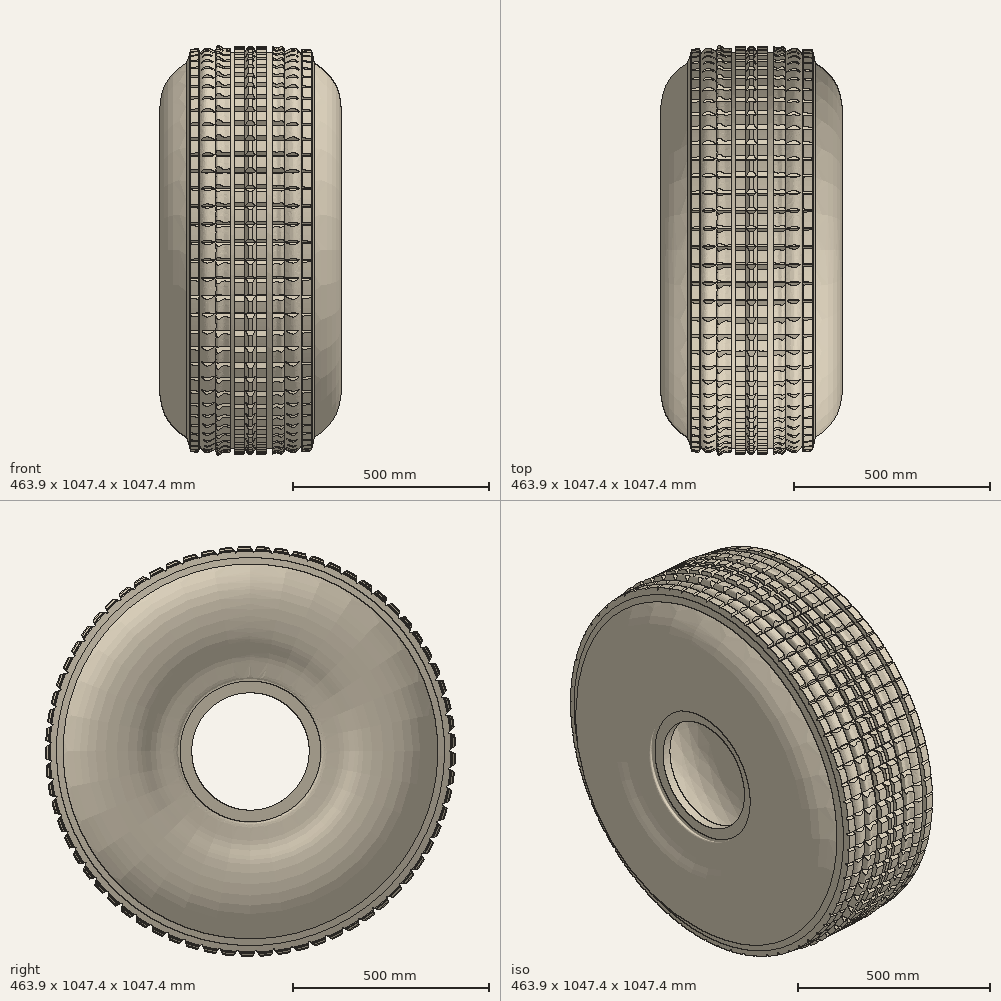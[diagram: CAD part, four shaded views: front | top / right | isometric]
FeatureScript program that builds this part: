
annotation { "Feature Type Name" : "Feature", "Feature Type Description" : "" }
export const myFeature = defineFeature(function(context is Context, id is Id, definition is map)
    precondition{}
    {
        {
            var Q0;
            Q0=qCreatedBy(makeId("Top.planeOp"),FACE);
            var sketch = newSketch(context, id + "F0", { "sketchPlane" : qUnion([Q0])});
            skPoint(sketch, "E0", {"position": v(-175, 150) * mm});
            skPoint(sketch, "E1", {"position": v(-150, 150) * mm});
            skLineSegment(sketch, "E2", {"start": v(-175, 150) * mm, "end": v(-150, 150) * mm});
            skPoint(sketch, "E3.MirrorP", {"position": v(150, 150) * mm});
            skPoint(sketch, "E4.MirrorP", {"position": v(175, 150) * mm});
            skLineSegment(sketch, "E5.MirrorCS", {"start": v(175, 150) * mm, "end": v(150, 150) * mm});
            skLineSegment(sketch, "E6", {"start": v(-175, 150) * mm, "end": v(-175, 180) * mm});
            skFitSpline(sketch, "E7", {"points": [v(-175, 180) * mm, v(-184.67, 184.02) * mm, v(-198.3, 234.45) * mm, v(-221.46, 282) * mm, v(-229.73, 382.86) * mm, v(-202.03, 445.7) * mm, v(-151.6, 486.2) * mm, v(0, 504.43) * mm], "startDerivative": vector(59.68, 901.94) * mm, "endDerivative": vector(1408.53, -72.4) * mm});
            skFitSpline(sketch, "E8", {"points": [v(0, 479.43) * mm, v(-134.36, 468.1) * mm, v(-182.95, 429.54) * mm, v(-201.89, 381.21) * mm, v(-198.6, 301.76) * mm, v(-176.16, 242.66) * mm, v(-163.87, 217.43) * mm, v(-150, 150) * mm], "startDerivative": vector(-727.82, -6.55) * mm, "endDerivative": vector(27.04, -741.2) * mm});
            skLineSegment(sketch, "E9.MirrorCS", {"start": v(175, 150) * mm, "end": v(175, 180) * mm});
            skFitSpline(sketch, "E10.MirrorCS", {"points": [v(175, 180) * mm, v(184.67, 184.02) * mm, v(198.3, 234.45) * mm, v(221.46, 282) * mm, v(229.73, 382.86) * mm, v(202.03, 445.7) * mm, v(151.6, 486.2) * mm, v(0, 504.43) * mm], "startDerivative": vector(-59.68, 901.94) * mm, "endDerivative": vector(-1408.53, -72.4) * mm});
            skFitSpline(sketch, "E11.MirrorCS", {"points": [v(0, 479.43) * mm, v(134.36, 468.1) * mm, v(182.95, 429.54) * mm, v(201.89, 381.21) * mm, v(198.6, 301.76) * mm, v(176.16, 242.66) * mm, v(163.87, 217.43) * mm, v(150, 150) * mm], "startDerivative": vector(727.82, -6.55) * mm, "endDerivative": vector(-27.04, -741.2) * mm});
            skLineSegment(sketch, "E12", {"start": v(-209.31, 0) * mm, "end": v(239.3, 0) * mm, "construction": true});
            skSolve(sketch);
        }
        {
            var Q0;
            Q0 = qSketchRegion(id + "F0", true);
            var Q1;
            Q1=sQuery(id+"F0.wireOp",EDGE,"E12");
            revolve(context, id + "F1", {"surfaceOperationType" : NewSurfaceOperationType.NEW, "entities" : qUnion([Q0]), "axis" : qUnion([Q1]), "revolveType" : RevolveType.FULL});
        }
        {
            var Q0;
            Q0=qCreatedBy(makeId("Top.planeOp"),FACE);
            var sketch = newSketch(context, id + "F2", { "sketchPlane" : qUnion([Q0])});
            skLineSegment(sketch, "E13.bottom", {"start": v(-130, 496.95) * mm, "end": v(-130, 496.95) * mm});
            skFitSpline(sketch, "E14", {"points": [v(-117.15, 514.71) * mm, v(-130, 496.95) * mm, v(-119.3, 500.26) * mm, v(-92.18, 504.71) * mm, v(-90.25, 504.85) * mm, v(-85.06, 505) * mm, v(-88.83, 507.25) * mm, v(-98.38, 513.06) * mm, v(-117.15, 514.71) * mm]});
            skLineSegment(sketch, "E15.MirrorCS", {"start": v(-40.33, 499.33) * mm, "end": v(-40.38, 521.13) * mm});
            skLineSegment(sketch, "E16.MirrorCS", {"start": v(-15, 499.38) * mm, "end": v(-14.97, 521.11) * mm});
            skLineSegment(sketch, "E17.MirrorCS", {"start": v(-40.33, 499.33) * mm, "end": v(-15, 499.38) * mm});
            skFitSpline(sketch, "E18.MirrorC", {"points": [v(-52.4, 516.54) * mm, v(-51.02, 508.2) * mm, v(-49.36, 501.85) * mm, v(-40.33, 499.33) * mm, v(-85.06, 505) * mm, v(-82.79, 523.58) * mm, v(-68.13, 515.76) * mm, v(-52.4, 516.54) * mm]});
            skLineSegment(sketch, "E19.MirrorCS", {"start": v(-40.38, 521.13) * mm, "end": v(-14.97, 521.11) * mm});
            skFitSpline(sketch, "E20.MirrorC", {"points": [v(55.63, 520.93) * mm, v(55.22, 506.03) * mm, v(40.33, 499.33) * mm, v(44.42, 498.82) * mm, v(85.82, 502.74) * mm, v(81.28, 520.6) * mm, v(67.8, 517.23) * mm, v(55.63, 520.93) * mm]});
            skPoint(sketch, "E21", {"position": v(130, 496.95) * mm});
            skLineSegment(sketch, "E22", {"start": v(-163.32, 478.74) * mm, "end": v(-156.87, 496.6) * mm});
            skLineSegment(sketch, "E23", {"start": v(-156.87, 496.6) * mm, "end": v(-152.6, 513.75) * mm});
            skLineSegment(sketch, "E24", {"start": v(-130, 496.95) * mm, "end": v(-163.32, 478.74) * mm});
            skLineSegment(sketch, "E25.MirrorCS", {"start": v(159.55, 495.78) * mm, "end": v(155.7, 512.1) * mm});
            skLineSegment(sketch, "E26.MirrorCS", {"start": v(163.38, 478.68) * mm, "end": v(159.55, 495.78) * mm});
            skLineSegment(sketch, "E27.MirrorCS", {"start": v(130, 496.95) * mm, "end": v(131.74, 514.48) * mm});
            skLineSegment(sketch, "E28.MirrorCS", {"start": v(130, 496.95) * mm, "end": v(163.38, 478.68) * mm});
            skFitSpline(sketch, "E29.MirrorC", {"points": [v(117.3, 514.36) * mm, v(130, 496.95) * mm, v(119.31, 500.29) * mm, v(107.79, 499.28) * mm, v(91.02, 502) * mm, v(87.1, 505.2) * mm, v(98.36, 513.14) * mm, v(117.3, 514.36) * mm]});
            skLineSegment(sketch, "E30", {"start": v(-15, 505.05) * mm, "end": v(-15, 499.38) * mm});
            skLineSegment(sketch, "E31", {"start": v(-15, 505.05) * mm, "end": v(-5.43, 520.92) * mm});
            skLineSegment(sketch, "E32", {"start": v(-5.43, 520.92) * mm, "end": v(5.22, 520.9) * mm});
            skLineSegment(sketch, "E33", {"start": v(5.22, 520.9) * mm, "end": v(15, 504.77) * mm});
            skLineSegment(sketch, "E34", {"start": v(15, 504.77) * mm, "end": v(0, 500.87) * mm});
            skLineSegment(sketch, "E35", {"start": v(0, 500.87) * mm, "end": v(-15, 505.05) * mm});
            skLineSegment(sketch, "E36.MirrorCS", {"start": v(15, 505.05) * mm, "end": v(15, 499.38) * mm});
            skLineSegment(sketch, "E37.MirrorCS", {"start": v(40.38, 521.13) * mm, "end": v(14.97, 521.11) * mm});
            skLineSegment(sketch, "E38.MirrorCS", {"start": v(40.33, 499.33) * mm, "end": v(15, 499.38) * mm});
            skLineSegment(sketch, "E39.MirrorCS", {"start": v(40.33, 499.33) * mm, "end": v(40.38, 521.13) * mm});
            skLineSegment(sketch, "E40.MirrorCS", {"start": v(15, 499.38) * mm, "end": v(14.97, 521.11) * mm});
            skLineSegment(sketch, "E41", {"start": v(-152.6, 513.75) * mm, "end": v(-132.3, 516.19) * mm});
            skLineSegment(sketch, "E42", {"start": v(-132.3, 516.19) * mm, "end": v(-130, 496.95) * mm});
            skLineSegment(sketch, "E43", {"start": v(131.74, 514.48) * mm, "end": v(155.7, 512.1) * mm});
            skSolve(sketch);
        }
        {
            var Q0;
            Q0 = qSketchRegion(id + "F2", true);
            var Q1;
            Q1=sQuery(id+"F0.wireOp",EDGE,"E12");
            revolve(context, id + "F3", {"operationType" : NewBodyOperationType.ADD, "surfaceOperationType" : NewSurfaceOperationType.NEW, "entities" : qUnion([Q0]), "axis" : qUnion([Q1]), "revolveType" : RevolveType.FULL});
        }
        {
            var Q0;
            Q0=qCreatedBy(makeId("Right.planeOp"),FACE);
            var sketch = newSketch(context, id + "F4", { "sketchPlane" : qUnion([Q0])});
            skLineSegment(sketch, "E44", {"start": v(532.3, 38.8) * mm, "end": v(504.85, 47.75) * mm});
            skLineSegment(sketch, "E45", {"start": v(504.85, 47.75) * mm, "end": v(526.33, 67.04) * mm});
            skLineSegment(sketch, "E46", {"start": v(526.33, 67.04) * mm, "end": v(532.3, 38.8) * mm});
            skPoint(sketch, "E47", {"position": v(504.85, 47.75) * mm});
            skLineSegment(sketch, "E48.1.0", {"start": v(526.56, 87.04) * mm, "end": v(498.42, 93.46) * mm});
            skLineSegment(sketch, "E48.1.1", {"start": v(498.42, 93.46) * mm, "end": v(518.05, 114.62) * mm});
            skLineSegment(sketch, "E48.1.2", {"start": v(518.05, 114.62) * mm, "end": v(526.56, 87.04) * mm});
            skLineSegment(sketch, "E48.2.0", {"start": v(516.47, 134.56) * mm, "end": v(487.86, 138.4) * mm});
            skLineSegment(sketch, "E48.2.1", {"start": v(487.86, 138.4) * mm, "end": v(505.48, 161.26) * mm});
            skLineSegment(sketch, "E48.2.2", {"start": v(505.48, 161.26) * mm, "end": v(516.47, 134.56) * mm});
            skLineSegment(sketch, "E48.3.0", {"start": v(502.1, 180.97) * mm, "end": v(473.25, 182.18) * mm});
            skLineSegment(sketch, "E48.3.1", {"start": v(473.25, 182.18) * mm, "end": v(488.72, 206.55) * mm});
            skLineSegment(sketch, "E48.3.2", {"start": v(488.72, 206.55) * mm, "end": v(502.1, 180.97) * mm});
            skLineSegment(sketch, "E48.4.0", {"start": v(483.56, 225.88) * mm, "end": v(454.72, 224.46) * mm});
            skLineSegment(sketch, "E48.4.1", {"start": v(454.72, 224.46) * mm, "end": v(467.92, 250.14) * mm});
            skLineSegment(sketch, "E48.4.2", {"start": v(467.92, 250.14) * mm, "end": v(483.56, 225.88) * mm});
            skLineSegment(sketch, "E48.5.0", {"start": v(461.01, 268.91) * mm, "end": v(432.43, 264.88) * mm});
            skLineSegment(sketch, "E48.5.1", {"start": v(432.43, 264.88) * mm, "end": v(443.23, 291.65) * mm});
            skLineSegment(sketch, "E48.5.2", {"start": v(443.23, 291.65) * mm, "end": v(461.01, 268.91) * mm});
            skLineSegment(sketch, "E48.6.0", {"start": v(434.65, 309.72) * mm, "end": v(406.55, 303.11) * mm});
            skLineSegment(sketch, "E48.6.1", {"start": v(406.55, 303.11) * mm, "end": v(414.87, 330.75) * mm});
            skLineSegment(sketch, "E48.6.2", {"start": v(414.87, 330.75) * mm, "end": v(434.65, 309.72) * mm});
            skLineSegment(sketch, "E48.7.0", {"start": v(404.68, 347.96) * mm, "end": v(377.3, 338.82) * mm});
            skLineSegment(sketch, "E48.7.1", {"start": v(377.3, 338.82) * mm, "end": v(383.08, 367.1) * mm});
            skLineSegment(sketch, "E48.7.2", {"start": v(383.08, 367.1) * mm, "end": v(404.68, 347.96) * mm});
            skLineSegment(sketch, "E48.8.0", {"start": v(371.36, 383.32) * mm, "end": v(344.93, 371.73) * mm});
            skLineSegment(sketch, "E48.8.1", {"start": v(344.93, 371.73) * mm, "end": v(348.1, 400.42) * mm});
            skLineSegment(sketch, "E48.8.2", {"start": v(348.1, 400.42) * mm, "end": v(371.36, 383.32) * mm});
            skLineSegment(sketch, "E48.9.0", {"start": v(334.97, 415.5) * mm, "end": v(309.7, 401.56) * mm});
            skLineSegment(sketch, "E48.9.1", {"start": v(309.7, 401.56) * mm, "end": v(310.25, 430.42) * mm});
            skLineSegment(sketch, "E48.9.2", {"start": v(310.25, 430.42) * mm, "end": v(334.97, 415.5) * mm});
            skLineSegment(sketch, "E48.10.0", {"start": v(295.8, 444.24) * mm, "end": v(271.9, 428.05) * mm});
            skLineSegment(sketch, "E48.10.1", {"start": v(271.9, 428.05) * mm, "end": v(269.83, 456.85) * mm});
            skLineSegment(sketch, "E48.10.2", {"start": v(269.83, 456.85) * mm, "end": v(295.8, 444.24) * mm});
            skLineSegment(sketch, "E48.11.0", {"start": v(254.18, 469.3) * mm, "end": v(231.84, 451) * mm});
            skLineSegment(sketch, "E48.11.1", {"start": v(231.84, 451) * mm, "end": v(227.17, 479.5) * mm});
            skLineSegment(sketch, "E48.11.2", {"start": v(227.17, 479.5) * mm, "end": v(254.18, 469.3) * mm});
            skLineSegment(sketch, "E48.12.0", {"start": v(210.45, 490.47) * mm, "end": v(189.87, 470.22) * mm});
            skLineSegment(sketch, "E48.12.1", {"start": v(189.87, 470.22) * mm, "end": v(182.62, 498.16) * mm});
            skLineSegment(sketch, "E48.12.2", {"start": v(182.62, 498.16) * mm, "end": v(210.45, 490.47) * mm});
            skLineSegment(sketch, "E48.13.0", {"start": v(164.97, 507.57) * mm, "end": v(146.33, 485.54) * mm});
            skLineSegment(sketch, "E48.13.1", {"start": v(146.33, 485.54) * mm, "end": v(136.57, 512.7) * mm});
            skLineSegment(sketch, "E48.13.2", {"start": v(136.57, 512.7) * mm, "end": v(164.97, 507.57) * mm});
            skLineSegment(sketch, "E48.14.0", {"start": v(118.13, 520.47) * mm, "end": v(101.57, 496.83) * mm});
            skLineSegment(sketch, "E48.14.1", {"start": v(101.57, 496.83) * mm, "end": v(89.38, 523) * mm});
            skLineSegment(sketch, "E48.14.2", {"start": v(89.38, 523) * mm, "end": v(118.13, 520.47) * mm});
            skLineSegment(sketch, "E48.15.0", {"start": v(70.32, 529.06) * mm, "end": v(55.97, 504) * mm});
            skLineSegment(sketch, "E48.15.1", {"start": v(55.97, 504) * mm, "end": v(41.45, 528.96) * mm});
            skLineSegment(sketch, "E48.15.2", {"start": v(41.45, 528.96) * mm, "end": v(70.32, 529.06) * mm});
            skLineSegment(sketch, "E48.16.0", {"start": v(21.91, 533.26) * mm, "end": v(9.9, 507) * mm});
            skLineSegment(sketch, "E48.16.1", {"start": v(9.9, 507) * mm, "end": v(-6.82, 530.54) * mm});
            skLineSegment(sketch, "E48.16.2", {"start": v(-6.82, 530.54) * mm, "end": v(21.91, 533.26) * mm});
            skLineSegment(sketch, "E48.17.0", {"start": v(-26.67, 533.04) * mm, "end": v(-36.24, 505.8) * mm});
            skLineSegment(sketch, "E48.17.1", {"start": v(-36.24, 505.8) * mm, "end": v(-55.04, 527.72) * mm});
            skLineSegment(sketch, "E48.17.2", {"start": v(-55.04, 527.72) * mm, "end": v(-26.67, 533.04) * mm});
            skLineSegment(sketch, "E48.18.0", {"start": v(-75.03, 528.4) * mm, "end": v(-82.09, 500.42) * mm});
            skLineSegment(sketch, "E48.18.1", {"start": v(-82.09, 500.42) * mm, "end": v(-102.8, 520.53) * mm});
            skLineSegment(sketch, "E48.18.2", {"start": v(-102.8, 520.53) * mm, "end": v(-75.03, 528.4) * mm});
            skLineSegment(sketch, "E48.19.0", {"start": v(-122.77, 519.4) * mm, "end": v(-127.25, 490.88) * mm});
            skLineSegment(sketch, "E48.19.1", {"start": v(-127.25, 490.88) * mm, "end": v(-149.7, 509.02) * mm});
            skLineSegment(sketch, "E48.19.2", {"start": v(-149.7, 509.02) * mm, "end": v(-122.77, 519.4) * mm});
            skLineSegment(sketch, "E48.20.0", {"start": v(-169.5, 506.08) * mm, "end": v(-171.36, 477.27) * mm});
            skLineSegment(sketch, "E48.20.1", {"start": v(-171.36, 477.27) * mm, "end": v(-195.38, 493.3) * mm});
            skLineSegment(sketch, "E48.20.2", {"start": v(-195.38, 493.3) * mm, "end": v(-169.5, 506.08) * mm});
            skLineSegment(sketch, "E48.21.0", {"start": v(-214.81, 488.57) * mm, "end": v(-214.06, 459.71) * mm});
            skLineSegment(sketch, "E48.21.1", {"start": v(-214.06, 459.71) * mm, "end": v(-239.42, 473.49) * mm});
            skLineSegment(sketch, "E48.21.2", {"start": v(-239.42, 473.49) * mm, "end": v(-214.81, 488.57) * mm});
            skLineSegment(sketch, "E48.22.0", {"start": v(-258.35, 467.01) * mm, "end": v(-254.97, 438.34) * mm});
            skLineSegment(sketch, "E48.22.1", {"start": v(-254.97, 438.34) * mm, "end": v(-281.49, 449.76) * mm});
            skLineSegment(sketch, "E48.22.2", {"start": v(-281.49, 449.76) * mm, "end": v(-258.35, 467.01) * mm});
            skLineSegment(sketch, "E48.23.0", {"start": v(-299.75, 441.59) * mm, "end": v(-293.78, 413.34) * mm});
            skLineSegment(sketch, "E48.23.1", {"start": v(-293.78, 413.34) * mm, "end": v(-321.22, 422.3) * mm});
            skLineSegment(sketch, "E48.23.2", {"start": v(-321.22, 422.3) * mm, "end": v(-299.75, 441.59) * mm});
            skLineSegment(sketch, "E48.24.0", {"start": v(-338.66, 412.5) * mm, "end": v(-330.15, 384.92) * mm});
            skLineSegment(sketch, "E48.24.1", {"start": v(-330.15, 384.92) * mm, "end": v(-358.3, 391.34) * mm});
            skLineSegment(sketch, "E48.24.2", {"start": v(-358.3, 391.34) * mm, "end": v(-338.66, 412.5) * mm});
            skLineSegment(sketch, "E48.25.0", {"start": v(-374.77, 380) * mm, "end": v(-363.78, 353.3) * mm});
            skLineSegment(sketch, "E48.25.1", {"start": v(-363.78, 353.3) * mm, "end": v(-392.4, 357.13) * mm});
            skLineSegment(sketch, "E48.25.2", {"start": v(-392.4, 357.13) * mm, "end": v(-374.77, 380) * mm});
            skLineSegment(sketch, "E48.26.0", {"start": v(-407.77, 344.34) * mm, "end": v(-394.4, 318.75) * mm});
            skLineSegment(sketch, "E48.26.1", {"start": v(-394.4, 318.75) * mm, "end": v(-423.24, 319.97) * mm});
            skLineSegment(sketch, "E48.26.2", {"start": v(-423.24, 319.97) * mm, "end": v(-407.77, 344.34) * mm});
            skLineSegment(sketch, "E48.27.0", {"start": v(-437.4, 305.83) * mm, "end": v(-421.75, 281.57) * mm});
            skLineSegment(sketch, "E48.27.1", {"start": v(-421.75, 281.57) * mm, "end": v(-450.59, 280.16) * mm});
            skLineSegment(sketch, "E48.27.2", {"start": v(-450.59, 280.16) * mm, "end": v(-437.4, 305.83) * mm});
            skLineSegment(sketch, "E48.28.0", {"start": v(-463.4, 264.8) * mm, "end": v(-445.61, 242.05) * mm});
            skLineSegment(sketch, "E48.28.1", {"start": v(-445.61, 242.05) * mm, "end": v(-474.2, 238.02) * mm});
            skLineSegment(sketch, "E48.28.2", {"start": v(-474.2, 238.02) * mm, "end": v(-463.4, 264.8) * mm});
            skLineSegment(sketch, "E48.29.0", {"start": v(-485.55, 221.56) * mm, "end": v(-465.78, 200.53) * mm});
            skLineSegment(sketch, "E48.29.1", {"start": v(-465.78, 200.53) * mm, "end": v(-493.88, 193.92) * mm});
            skLineSegment(sketch, "E48.29.2", {"start": v(-493.88, 193.92) * mm, "end": v(-485.55, 221.56) * mm});
            skLineSegment(sketch, "E48.30.0", {"start": v(-503.69, 176.49) * mm, "end": v(-482.08, 157.34) * mm});
            skLineSegment(sketch, "E48.30.1", {"start": v(-482.08, 157.34) * mm, "end": v(-509.46, 148.2) * mm});
            skLineSegment(sketch, "E48.30.2", {"start": v(-509.46, 148.2) * mm, "end": v(-503.69, 176.49) * mm});
            skLineSegment(sketch, "E48.31.0", {"start": v(-517.65, 129.95) * mm, "end": v(-494.4, 112.85) * mm});
            skLineSegment(sketch, "E48.31.1", {"start": v(-494.4, 112.85) * mm, "end": v(-520.83, 101.26) * mm});
            skLineSegment(sketch, "E48.31.2", {"start": v(-520.83, 101.26) * mm, "end": v(-517.65, 129.95) * mm});
            skLineSegment(sketch, "E48.32.0", {"start": v(-527.32, 82.34) * mm, "end": v(-502.6, 67.43) * mm});
            skLineSegment(sketch, "E48.32.1", {"start": v(-502.6, 67.43) * mm, "end": v(-527.88, 53.48) * mm});
            skLineSegment(sketch, "E48.32.2", {"start": v(-527.88, 53.48) * mm, "end": v(-527.32, 82.34) * mm});
            skLineSegment(sketch, "E48.33.0", {"start": v(-532.62, 34.05) * mm, "end": v(-506.65, 21.44) * mm});
            skLineSegment(sketch, "E48.33.1", {"start": v(-506.65, 21.44) * mm, "end": v(-530.56, 5.25) * mm});
            skLineSegment(sketch, "E48.33.2", {"start": v(-530.56, 5.25) * mm, "end": v(-532.62, 34.05) * mm});
            skLineSegment(sketch, "E48.34.0", {"start": v(-533.51, -14.53) * mm, "end": v(-506.5, -24.72) * mm});
            skLineSegment(sketch, "E48.34.1", {"start": v(-506.5, -24.72) * mm, "end": v(-528.83, -43.01) * mm});
            skLineSegment(sketch, "E48.34.2", {"start": v(-528.83, -43.01) * mm, "end": v(-533.51, -14.53) * mm});
            skLineSegment(sketch, "E48.35.0", {"start": v(-529.98, -62.98) * mm, "end": v(-502.16, -70.68) * mm});
            skLineSegment(sketch, "E48.35.1", {"start": v(-502.16, -70.68) * mm, "end": v(-522.73, -90.92) * mm});
            skLineSegment(sketch, "E48.35.2", {"start": v(-522.73, -90.92) * mm, "end": v(-529.98, -62.98) * mm});
            skLineSegment(sketch, "E48.36.0", {"start": v(-522.06, -110.91) * mm, "end": v(-493.65, -116.05) * mm});
            skLineSegment(sketch, "E48.36.1", {"start": v(-493.65, -116.05) * mm, "end": v(-512.3, -138.08) * mm});
            skLineSegment(sketch, "E48.36.2", {"start": v(-512.3, -138.08) * mm, "end": v(-522.06, -110.91) * mm});
            skLineSegment(sketch, "E48.37.0", {"start": v(-509.8, -157.93) * mm, "end": v(-481.05, -160.46) * mm});
            skLineSegment(sketch, "E48.37.1", {"start": v(-481.05, -160.46) * mm, "end": v(-497.62, -184.1) * mm});
            skLineSegment(sketch, "E48.37.2", {"start": v(-497.62, -184.1) * mm, "end": v(-509.8, -157.93) * mm});
            skLineSegment(sketch, "E48.38.0", {"start": v(-493.34, -203.63) * mm, "end": v(-464.47, -203.54) * mm});
            skLineSegment(sketch, "E48.38.1", {"start": v(-464.47, -203.54) * mm, "end": v(-478.82, -228.58) * mm});
            skLineSegment(sketch, "E48.38.2", {"start": v(-478.82, -228.58) * mm, "end": v(-493.34, -203.63) * mm});
            skLineSegment(sketch, "E48.39.0", {"start": v(-472.77, -247.65) * mm, "end": v(-444.03, -244.93) * mm});
            skLineSegment(sketch, "E48.39.1", {"start": v(-444.03, -244.93) * mm, "end": v(-456.05, -271.18) * mm});
            skLineSegment(sketch, "E48.39.2", {"start": v(-456.05, -271.18) * mm, "end": v(-472.77, -247.65) * mm});
            skLineSegment(sketch, "E48.40.0", {"start": v(-448.3, -289.62) * mm, "end": v(-419.92, -284.3) * mm});
            skLineSegment(sketch, "E48.40.1", {"start": v(-419.92, -284.3) * mm, "end": v(-429.5, -311.53) * mm});
            skLineSegment(sketch, "E48.40.2", {"start": v(-429.5, -311.53) * mm, "end": v(-448.3, -289.62) * mm});
            skLineSegment(sketch, "E48.41.0", {"start": v(-420.1, -329.18) * mm, "end": v(-392.33, -321.3) * mm});
            skLineSegment(sketch, "E48.41.1", {"start": v(-392.33, -321.3) * mm, "end": v(-399.39, -349.3) * mm});
            skLineSegment(sketch, "E48.41.2", {"start": v(-399.39, -349.3) * mm, "end": v(-420.1, -329.18) * mm});
            skLineSegment(sketch, "E48.42.0", {"start": v(-388.43, -366.02) * mm, "end": v(-361.49, -355.65) * mm});
            skLineSegment(sketch, "E48.42.1", {"start": v(-361.49, -355.65) * mm, "end": v(-365.97, -384.16) * mm});
            skLineSegment(sketch, "E48.42.2", {"start": v(-365.97, -384.16) * mm, "end": v(-388.43, -366.02) * mm});
            skLineSegment(sketch, "E48.43.0", {"start": v(-353.53, -399.83) * mm, "end": v(-327.65, -387.04) * mm});
            skLineSegment(sketch, "E48.43.1", {"start": v(-327.65, -387.04) * mm, "end": v(-329.52, -415.85) * mm});
            skLineSegment(sketch, "E48.43.2", {"start": v(-329.52, -415.85) * mm, "end": v(-353.53, -399.83) * mm});
            skLineSegment(sketch, "E48.44.0", {"start": v(-315.71, -430.32) * mm, "end": v(-291.1, -415.23) * mm});
            skLineSegment(sketch, "E48.44.1", {"start": v(-291.1, -415.23) * mm, "end": v(-290.34, -444.1) * mm});
            skLineSegment(sketch, "E48.44.2", {"start": v(-290.34, -444.1) * mm, "end": v(-315.71, -430.32) * mm});
            skLineSegment(sketch, "E48.45.0", {"start": v(-275.27, -457.24) * mm, "end": v(-252.13, -439.99) * mm});
            skLineSegment(sketch, "E48.45.1", {"start": v(-252.13, -439.99) * mm, "end": v(-248.76, -468.65) * mm});
            skLineSegment(sketch, "E48.45.2", {"start": v(-248.76, -468.65) * mm, "end": v(-275.27, -457.24) * mm});
            skLineSegment(sketch, "E48.46.0", {"start": v(-232.55, -480.38) * mm, "end": v(-211.08, -461.09) * mm});
            skLineSegment(sketch, "E48.46.1", {"start": v(-211.08, -461.09) * mm, "end": v(-205.1, -489.33) * mm});
            skLineSegment(sketch, "E48.46.2", {"start": v(-205.1, -489.33) * mm, "end": v(-232.55, -480.38) * mm});
            skLineSegment(sketch, "E48.47.0", {"start": v(-187.9, -499.54) * mm, "end": v(-168.27, -478.37) * mm});
            skLineSegment(sketch, "E48.47.1", {"start": v(-168.27, -478.37) * mm, "end": v(-159.76, -505.96) * mm});
            skLineSegment(sketch, "E48.47.2", {"start": v(-159.76, -505.96) * mm, "end": v(-187.9, -499.54) * mm});
            skLineSegment(sketch, "E48.48.0", {"start": v(-141.7, -514.55) * mm, "end": v(-124.07, -491.7) * mm});
            skLineSegment(sketch, "E48.48.1", {"start": v(-124.07, -491.7) * mm, "end": v(-113.09, -518.39) * mm});
            skLineSegment(sketch, "E48.48.2", {"start": v(-113.09, -518.39) * mm, "end": v(-141.7, -514.55) * mm});
            skLineSegment(sketch, "E48.49.0", {"start": v(-94.32, -525.3) * mm, "end": v(-78.85, -500.94) * mm});
            skLineSegment(sketch, "E48.49.1", {"start": v(-78.85, -500.94) * mm, "end": v(-65.48, -526.52) * mm});
            skLineSegment(sketch, "E48.49.2", {"start": v(-65.48, -526.52) * mm, "end": v(-94.32, -525.3) * mm});
            skLineSegment(sketch, "E48.50.0", {"start": v(-46.16, -531.7) * mm, "end": v(-32.97, -506.03) * mm});
            skLineSegment(sketch, "E48.50.1", {"start": v(-32.97, -506.03) * mm, "end": v(-17.33, -530.3) * mm});
            skLineSegment(sketch, "E48.50.2", {"start": v(-17.33, -530.3) * mm, "end": v(-46.16, -531.7) * mm});
            skLineSegment(sketch, "E48.51.0", {"start": v(2.38, -533.7) * mm, "end": v(13.18, -506.94) * mm});
            skLineSegment(sketch, "E48.51.1", {"start": v(13.18, -506.94) * mm, "end": v(30.96, -529.68) * mm});
            skLineSegment(sketch, "E48.51.2", {"start": v(30.96, -529.68) * mm, "end": v(2.38, -533.7) * mm});
            skLineSegment(sketch, "E48.52.0", {"start": v(50.9, -531.28) * mm, "end": v(59.23, -503.64) * mm});
            skLineSegment(sketch, "E48.52.1", {"start": v(59.23, -503.64) * mm, "end": v(79, -524.67) * mm});
            skLineSegment(sketch, "E48.52.2", {"start": v(79, -524.67) * mm, "end": v(50.9, -531.28) * mm});
            skLineSegment(sketch, "E48.53.0", {"start": v(99, -524.45) * mm, "end": v(104.78, -496.16) * mm});
            skLineSegment(sketch, "E48.53.1", {"start": v(104.78, -496.16) * mm, "end": v(126.39, -515.3) * mm});
            skLineSegment(sketch, "E48.53.2", {"start": v(126.39, -515.3) * mm, "end": v(99, -524.45) * mm});
            skLineSegment(sketch, "E48.54.0", {"start": v(146.28, -513.27) * mm, "end": v(149.46, -484.58) * mm});
            skLineSegment(sketch, "E48.54.1", {"start": v(149.46, -484.58) * mm, "end": v(172.72, -501.68) * mm});
            skLineSegment(sketch, "E48.54.2", {"start": v(172.72, -501.68) * mm, "end": v(146.28, -513.27) * mm});
            skLineSegment(sketch, "E48.55.0", {"start": v(192.35, -497.84) * mm, "end": v(192.91, -468.98) * mm});
            skLineSegment(sketch, "E48.55.1", {"start": v(192.91, -468.98) * mm, "end": v(217.63, -483.9) * mm});
            skLineSegment(sketch, "E48.55.2", {"start": v(217.63, -483.9) * mm, "end": v(192.35, -497.84) * mm});
            skLineSegment(sketch, "E48.56.0", {"start": v(236.82, -478.29) * mm, "end": v(234.76, -449.5) * mm});
            skLineSegment(sketch, "E48.56.1", {"start": v(234.76, -449.5) * mm, "end": v(260.73, -462.1) * mm});
            skLineSegment(sketch, "E48.56.2", {"start": v(260.73, -462.1) * mm, "end": v(236.82, -478.29) * mm});
            skLineSegment(sketch, "E48.57.0", {"start": v(279.34, -454.77) * mm, "end": v(274.66, -426.29) * mm});
            skLineSegment(sketch, "E48.57.1", {"start": v(274.66, -426.29) * mm, "end": v(301.67, -436.48) * mm});
            skLineSegment(sketch, "E48.57.2", {"start": v(301.67, -436.48) * mm, "end": v(279.34, -454.77) * mm});
            skLineSegment(sketch, "E48.58.0", {"start": v(319.53, -427.49) * mm, "end": v(312.29, -399.54) * mm});
            skLineSegment(sketch, "E48.58.1", {"start": v(312.29, -399.54) * mm, "end": v(340.1, -407.24) * mm});
            skLineSegment(sketch, "E48.58.2", {"start": v(340.1, -407.24) * mm, "end": v(319.53, -427.49) * mm});
            skLineSegment(sketch, "E48.59.0", {"start": v(357.08, -396.66) * mm, "end": v(347.32, -369.49) * mm});
            skLineSegment(sketch, "E48.59.1", {"start": v(347.32, -369.49) * mm, "end": v(375.73, -374.62) * mm});
            skLineSegment(sketch, "E48.59.2", {"start": v(375.73, -374.62) * mm, "end": v(357.08, -396.66) * mm});
            skPoint(sketch, "E48.center", {"position": v(0, 0) * mm});
            skLineSegment(sketch, "E49.2.60.0", {"start": v(391.67, -362.54) * mm, "end": v(379.48, -336.38) * mm});
            skLineSegment(sketch, "E49.3.60.0", {"start": v(379.48, -336.38) * mm, "end": v(408.24, -338.9) * mm});
            skLineSegment(sketch, "E49.6.60.0", {"start": v(408.24, -338.9) * mm, "end": v(391.67, -362.54) * mm});
            skLineSegment(sketch, "E49.2.61.0", {"start": v(423.02, -325.42) * mm, "end": v(408.5, -300.47) * mm});
            skLineSegment(sketch, "E49.3.61.0", {"start": v(408.5, -300.47) * mm, "end": v(437.37, -300.38) * mm});
            skLineSegment(sketch, "E49.6.61.0", {"start": v(437.37, -300.38) * mm, "end": v(423.02, -325.42) * mm});
            skLineSegment(sketch, "E49.2.62.0", {"start": v(450.86, -285.6) * mm, "end": v(434.13, -262.08) * mm});
            skLineSegment(sketch, "E49.3.62.0", {"start": v(434.13, -262.08) * mm, "end": v(462.87, -259.36) * mm});
            skLineSegment(sketch, "E49.6.62.0", {"start": v(462.87, -259.36) * mm, "end": v(450.86, -285.6) * mm});
            skLineSegment(sketch, "E49.2.63.0", {"start": v(474.96, -243.43) * mm, "end": v(456.17, -221.52) * mm});
            skLineSegment(sketch, "E49.3.63.0", {"start": v(456.17, -221.52) * mm, "end": v(484.54, -216.2) * mm});
            skLineSegment(sketch, "E49.6.63.0", {"start": v(484.54, -216.2) * mm, "end": v(474.96, -243.43) * mm});
            skLineSegment(sketch, "E49.2.64.0", {"start": v(495.13, -199.23) * mm, "end": v(474.42, -179.12) * mm});
            skLineSegment(sketch, "E49.3.64.0", {"start": v(474.42, -179.12) * mm, "end": v(502.19, -171.24) * mm});
            skLineSegment(sketch, "E49.6.64.0", {"start": v(502.19, -171.24) * mm, "end": v(495.13, -199.23) * mm});
            skLineSegment(sketch, "E50.2.65.0", {"start": v(511.2, -153.38) * mm, "end": v(488.74, -135.24) * mm});
            skLineSegment(sketch, "E50.3.65.0", {"start": v(488.74, -135.24) * mm, "end": v(515.68, -124.86) * mm});
            skLineSegment(sketch, "E50.6.65.0", {"start": v(515.68, -124.86) * mm, "end": v(511.2, -153.38) * mm});
            skLineSegment(sketch, "E50.2.66.0", {"start": v(523.03, -106.26) * mm, "end": v(499.01, -90.23) * mm});
            skLineSegment(sketch, "E50.3.66.0", {"start": v(499.01, -90.23) * mm, "end": v(524.9, -77.45) * mm});
            skLineSegment(sketch, "E50.6.66.0", {"start": v(524.9, -77.45) * mm, "end": v(523.03, -106.26) * mm});
            skLineSegment(sketch, "E50.2.67.0", {"start": v(530.52, -58.25) * mm, "end": v(505.15, -44.48) * mm});
            skLineSegment(sketch, "E50.3.67.0", {"start": v(505.15, -44.48) * mm, "end": v(529.77, -29.4) * mm});
            skLineSegment(sketch, "E50.6.67.0", {"start": v(529.77, -29.4) * mm, "end": v(530.52, -58.25) * mm});
            skLineSegment(sketch, "E51.2.68.0", {"start": v(533.62, -9.77) * mm, "end": v(507.1, 1.64) * mm});
            skLineSegment(sketch, "E51.3.68.0", {"start": v(507.1, 1.64) * mm, "end": v(530.24, 18.9) * mm});
            skLineSegment(sketch, "E51.6.68.0", {"start": v(530.24, 18.9) * mm, "end": v(533.62, -9.77) * mm});
            skSolve(sketch);
        }
        {
            var Q0;
            Q0 = qSketchRegion(id + "F4", true);
            extrude(context, id + "F5", {"entities" : qUnion([Q0]), "operationType" : NewBodyOperationType.REMOVE, "endBound" : BoundingType.SYMMETRIC, "oppositeDirection" : true, "depth" : 320 * mm, "offsetDistance" : 25 * mm});
        }
    });
